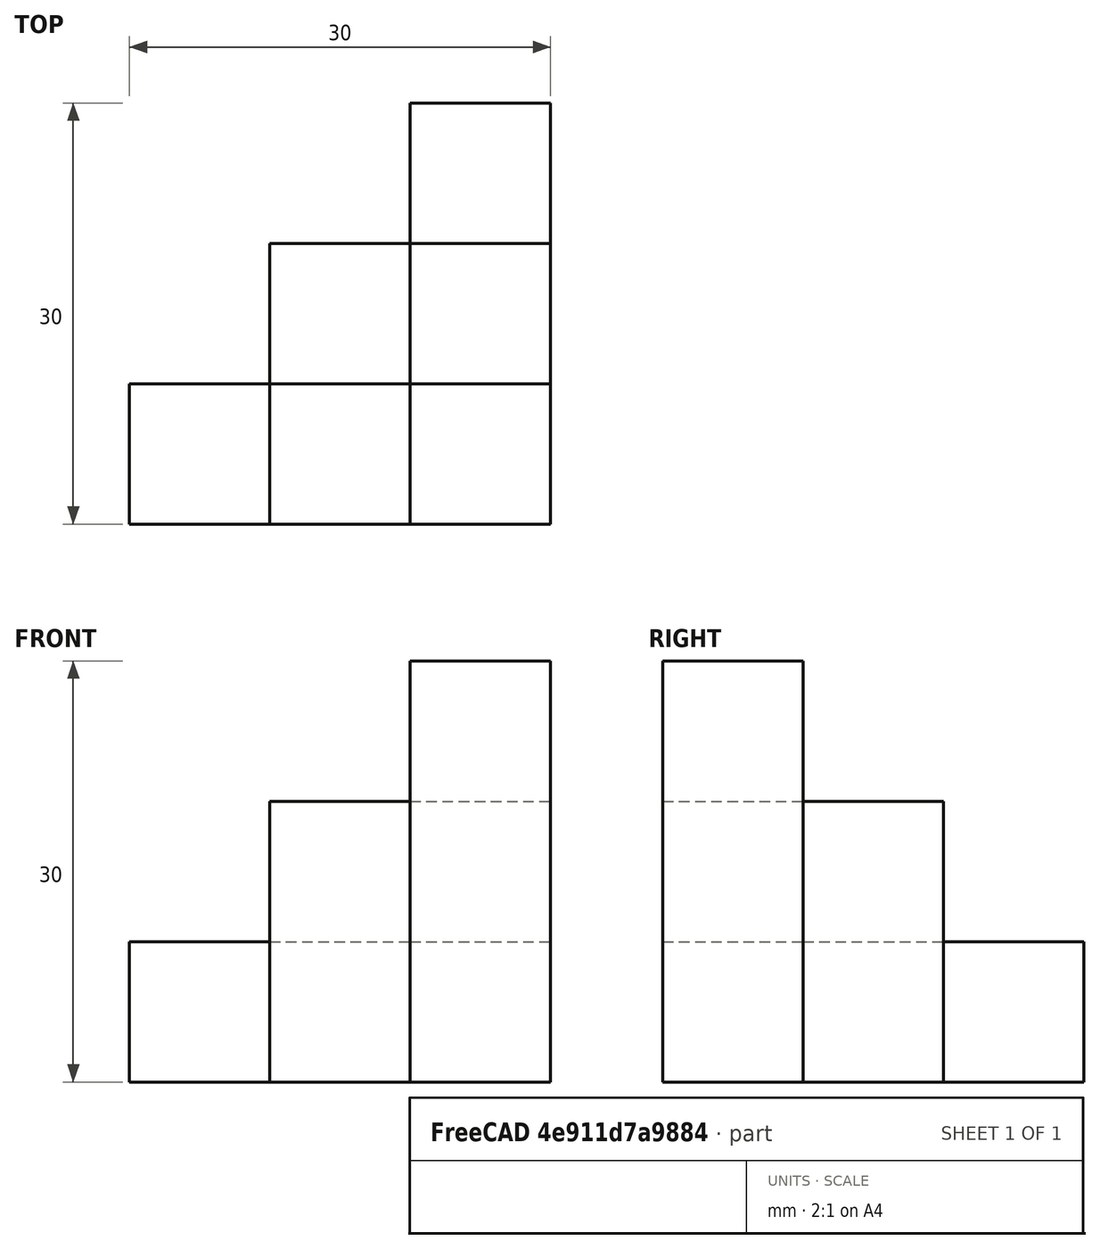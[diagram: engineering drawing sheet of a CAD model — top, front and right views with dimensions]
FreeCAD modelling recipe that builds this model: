
FCSTD DOCUMENT  (FreeCAD 0.21R33694 (Git))
Label: OJT1_T04R01_qubert2
License: All rights reserved
LicenseURL: https://en.wikipedia.org/wiki/All_rights_reserved
objects: Part::Box×6
note: 6 computed .brp shape members not serialized (recipe doc carries the construction recipe); baked Part::Feature solids carry a one-line shape summary decoded from their .brp

FEATURE [Part::Box] Box  label="Cub"
  AttacherType = Attacher::AttachEngine3D
  Height = 10
  Length = 10
  Placement = pos=(-10,0,0) rot=(0,0,1;0rad)
  Width = 10
FEATURE [Part::Box] Box003  label="Cub003"
  AttacherType = Attacher::AttachEngine3D
  Height = 20
  Length = 10
  Placement = pos=(10,10,0) rot=(0,0,1;0rad)
  Width = 10
FEATURE [Part::Box] Box005  label="Cub005"
  AttacherType = Attacher::AttachEngine3D
  Height = 30
  Length = 10
  Placement = pos=(10,0,0) rot=(0,0,1;0rad)
  Width = 10
FEATURE [Part::Box] Box007  label="Cub007"
  AttacherType = Attacher::AttachEngine3D
  Height = 20
  Length = 10
  Width = 10
FEATURE [Part::Box] Box008  label="Cub008"
  AttacherType = Attacher::AttachEngine3D
  Height = 10
  Length = 10
  Placement = pos=(0,10,0) rot=(0,0,1;0rad)
  Width = 10
FEATURE [Part::Box] Box009  label="Cub009"
  AttacherType = Attacher::AttachEngine3D
  Height = 10
  Length = 10
  Placement = pos=(10,20,0) rot=(0,0,1;0rad)
  Width = 10
